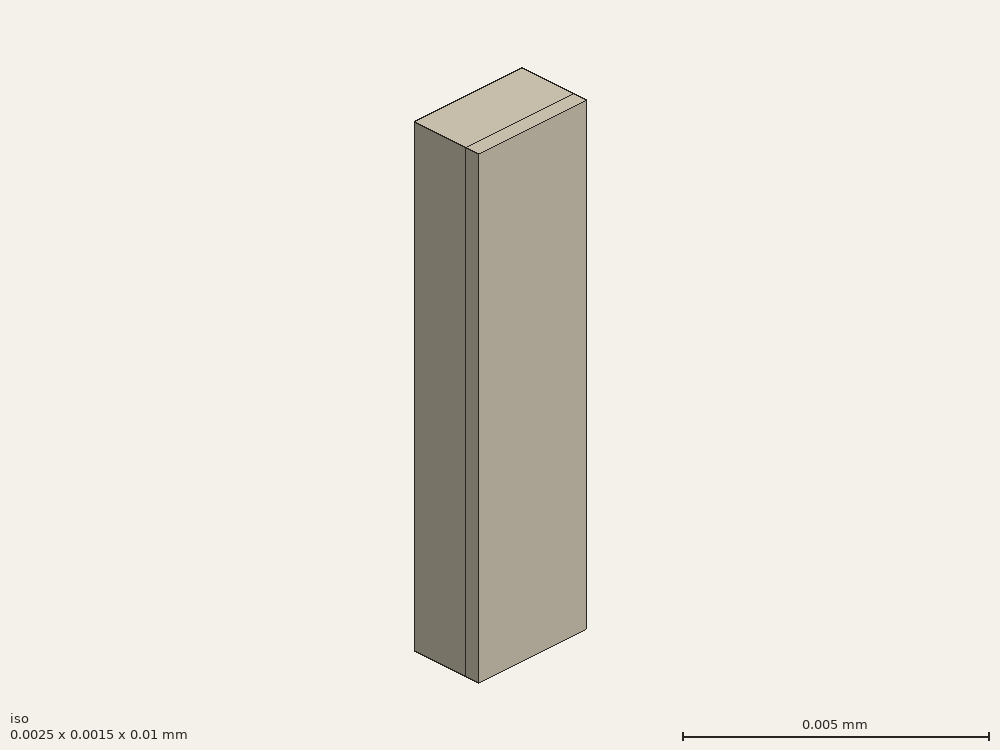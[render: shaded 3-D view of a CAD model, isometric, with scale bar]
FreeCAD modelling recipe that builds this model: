
FCSTD DOCUMENT  (FreeCAD 0.21R33694 (Git))
Label: microstrip_step
License: All rights reserved
LicenseURL: http://en.wikipedia.org/wiki/All_rights_reserved
objects: Part::Part2DObjectPython×10, App::FeaturePython×6, Part::Extrusion×4, Part::Cut×2, Part::FeaturePython×1
note: 17 computed .brp shape members not serialized (recipe doc carries the construction recipe); baked Part::Feature solids carry a one-line shape summary decoded from their .brp

FEATURE [Part::Part2DObjectPython] Rectangle  label="substrate2D"  # Draft 2D object (typed FeaturePython)
  Area = 6.4516e-07
  ChamferSize = 0
  Columns = 1
  FilletRadius = 0
  Height = 0.000254
  Length = 0.00254
  MakeFace = true
  Rows = 1
FEATURE [Part::Part2DObjectPython] Rectangle001  label="input2D"  # Draft 2D object (typed FeaturePython)
  Area = 6.35e-09
  ChamferSize = 0
  Columns = 1
  FilletRadius = 0
  Height = 2.5e-05
  Length = 0.000254
  MakeFace = true
  Placement = pos=(0.001143,0.000254,0) rot=(0,0,1;0rad)
  Rows = 1
FEATURE [Part::Part2DObjectPython] Rectangle002  label="output2D"  # Draft 2D object (typed FeaturePython)
  Area = 1.27e-08
  ChamferSize = 0
  Columns = 1
  FilletRadius = 0
  Height = 2.5e-05
  Length = 0.000508
  MakeFace = true
  Placement = pos=(0.001016,0.000254,0) rot=(0,0,1;0rad)
  Rows = 1
FEATURE [Part::Part2DObjectPython] Rectangle003  label="air2D"  # Draft 2D object (typed FeaturePython)
  Area = 3.2258e-06
  ChamferSize = 0
  Columns = 1
  FilletRadius = 0
  Height = 0.00127
  Length = 0.00254
  MakeFace = true
  Placement = pos=(0,0.000254,0) rot=(0,0,1;0rad)
  Rows = 1
FEATURE [Part::Extrusion] Extrude  label="substrate"
  Base = -> Rectangle
  Dir = (0,0,1)
  DirMode = 2
  FaceMakerClass = Part::FaceMakerBullseye
  LengthFwd = 0.01
  LengthRev = 0
  Solid = false
  Symmetric = false
FEATURE [Part::Extrusion] Extrude001  label="input"
  Base = -> Rectangle001
  Dir = (0,0,1)
  DirMode = 2
  FaceMakerClass = Part::FaceMakerBullseye
  LengthFwd = 0.005
  LengthRev = 0
  Solid = false
  Symmetric = false
FEATURE [Part::Extrusion] Extrude002  label="output"
  Base = -> Rectangle002
  Dir = (0,0,1)
  DirMode = 2
  FaceMakerClass = Part::FaceMakerBullseye
  LengthFwd = 0.005
  LengthRev = 0
  Placement = pos=(0,0,0.005) rot=(0,0,1;0rad)
  Solid = false
  Symmetric = false
FEATURE [Part::Extrusion] Extrude003  label="air"
  Base = -> Rectangle003
  Dir = (0,0,1)
  DirMode = 2
  FaceMakerClass = Part::FaceMakerBullseye
  LengthFwd = 0.01
  LengthRev = 0
  Solid = false
  Symmetric = false
FEATURE [Part::Cut] Cut
  Base = -> Extrude003
  Tool = -> Extrude001
FEATURE [Part::Cut] Cut001  label="air_metal"
  Base = -> Cut
  Tool = -> Extrude002
FEATURE [Part::Part2DObjectPython] Rectangle004  label="_Pportout"  # Draft 2D object (typed FeaturePython)
  Area = 3.87096e-06
  ChamferSize = 0
  Columns = 1
  FilletRadius = 0
  Height = 0.001524
  Length = 0.00254
  MakeFace = true
  Placement = pos=(0,0,0.01) rot=(0,0,1;0rad)
  Rows = 1
FEATURE [Part::Part2DObjectPython] Rectangle005  label="_PIout"  # Draft 2D object (typed FeaturePython)
  Area = 1.27e-08
  ChamferSize = 0
  Columns = 1
  FilletRadius = 0
  Height = 2.5e-05
  Length = 0.000508
  MakeFace = true
  Placement = pos=(0.001016,0.000254,0.01) rot=(0,0,1;0rad)
  Rows = 1
FEATURE [Part::Part2DObjectPython] Line  label="_PVout"  # Draft 2D object (typed FeaturePython)
  Area = 0
  ChamferSize = 0
  Closed = false
  End = (0.00127,0.000254,0.01)
  FilletRadius = 0
  Length = 0.000254
  MakeFace = true
  Placement = pos=(0.00127,0,0.01) rot=(0,0,1;0rad)
  Points = (2) [(0,0,0),(0,0.000254,0)]
  Start = (0.00127,0,0.01)
  Subdivisions = 0
FEATURE [Part::Part2DObjectPython] Rectangle006  label="_Pportin"  # Draft 2D object (typed FeaturePython)
  Area = 3.87096e-06
  ChamferSize = 0
  Columns = 1
  FilletRadius = 0
  Height = 0.00254
  Length = 0.001524
  MakeFace = true
  Placement = pos=(0,0,0) rot=(0.707107,0.707107,0;3.14159rad)
  Rows = 1
FEATURE [Part::Part2DObjectPython] Rectangle007  label="_PIin"  # Draft 2D object (typed FeaturePython)
  Area = 6.35e-09
  ChamferSize = 0
  Columns = 1
  FilletRadius = 0
  Height = 0.000254
  Length = 2.5e-05
  MakeFace = true
  Placement = pos=(0.001143,0.000254,0) rot=(0.707107,0.707107,0;3.14159rad)
  Rows = 1
FEATURE [Part::Part2DObjectPython] Line001  label="_PVin"  # Draft 2D object (typed FeaturePython)
  Area = 0
  ChamferSize = 0
  Closed = false
  End = (0.00127,0.000254,0)
  FilletRadius = 0
  Length = 0.000254
  MakeFace = true
  Placement = pos=(0.00127,0,0) rot=(0.707107,0.707107,0;3.14159rad)
  Points = (2) [(0,0,0),(0.000254,2.1684e-19,0)]
  Start = (0.00127,0,0)
  Subdivisions = 0
FEATURE [App::FeaturePython] Text  label="_Sin(PV){portin}"  # WARN: FeaturePython — macro-defined, semantics opaque (R4)
  Placement = pos=(0.00299776,0.00995601,0) rot=(0.707107,0.707107,0;3.14159rad)
  Text = .
FEATURE [App::FeaturePython] Text001  label="_Min(1,current){Iin}"  # WARN: FeaturePython — macro-defined, semantics opaque (R4)
  Placement = pos=(0.00299776,0.00995601,0) rot=(0.707107,0.707107,0;3.14159rad)
  Text = .
FEATURE [App::FeaturePython] Text002  label="_Min(1,voltage){Vin}"  # WARN: FeaturePython — macro-defined, semantics opaque (R4)
  Placement = pos=(0.00299776,0.00995601,0) rot=(0.707107,0.707107,0;3.14159rad)
  Text = .
FEATURE [App::FeaturePython] Text003  label="_Sout(PV){portout}"  # WARN: FeaturePython — macro-defined, semantics opaque (R4)
  Placement = pos=(0.00299776,0.00995601,0) rot=(0.707107,0.707107,0;3.14159rad)
  Text = .
FEATURE [App::FeaturePython] Text004  label="_Mout(2,current){Iout}"  # WARN: FeaturePython — macro-defined, semantics opaque (R4)
  Placement = pos=(0.00299776,0.00995601,0) rot=(0.707107,0.707107,0;3.14159rad)
  Text = .
FEATURE [App::FeaturePython] Text005  label="_Mout(2,voltage){Vout}"  # WARN: FeaturePython — macro-defined, semantics opaque (R4)
  Placement = pos=(0.00299776,0.00995601,0) rot=(0.707107,0.707107,0;3.14159rad)
  Text = .
FEATURE [Part::FeaturePython] BooleanFragments  # WARN: FeaturePython — macro-defined, semantics opaque (R4)
  Mode = 0
  Objects = -> [Extrude,Cut001]
  Tolerance = 0
